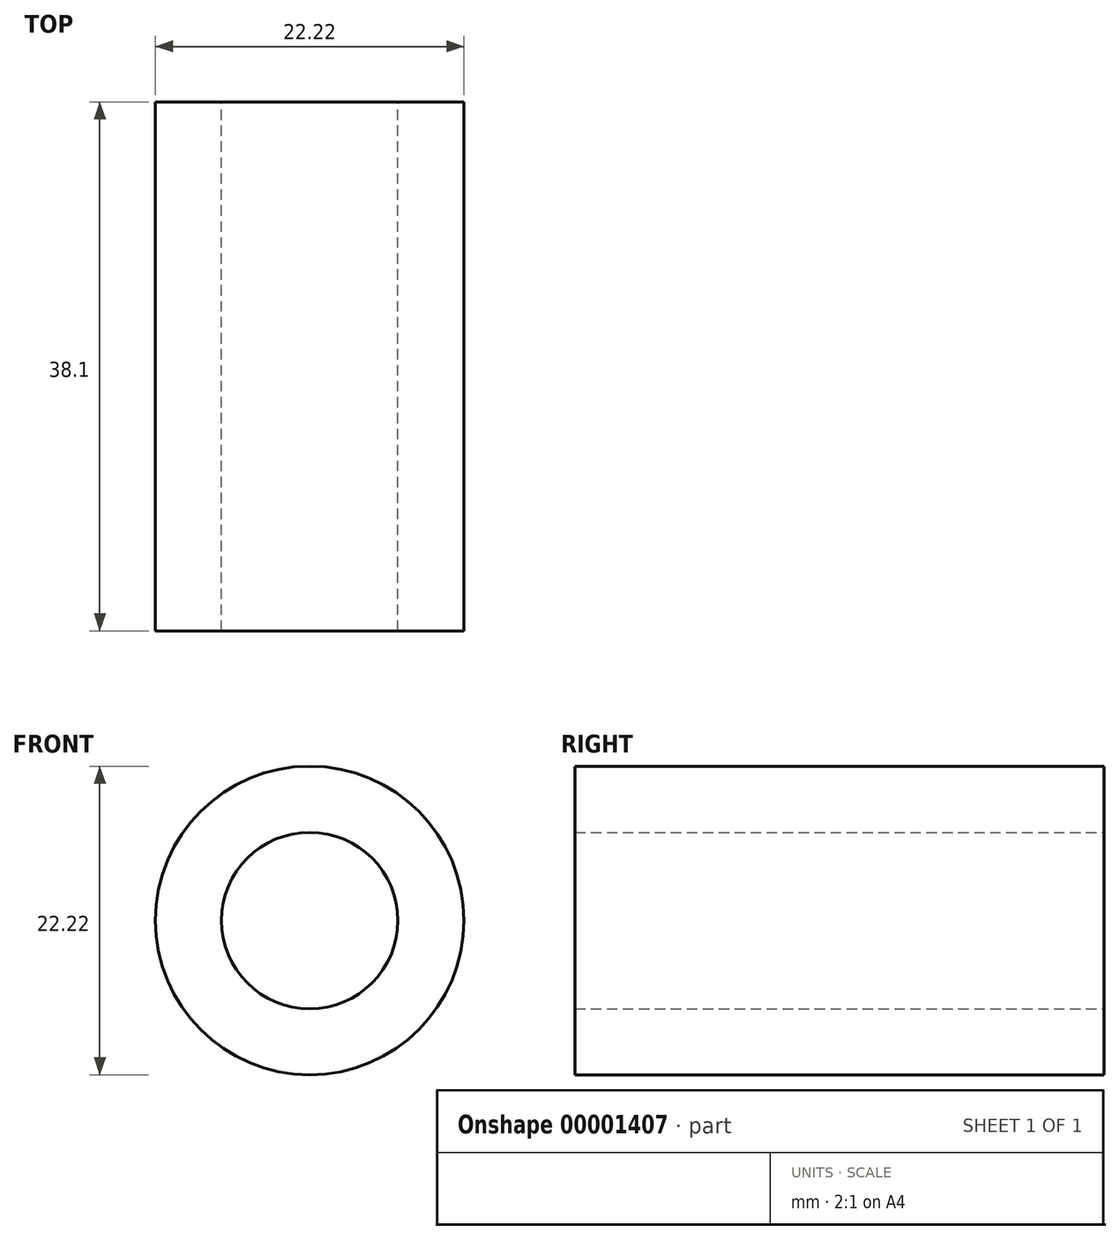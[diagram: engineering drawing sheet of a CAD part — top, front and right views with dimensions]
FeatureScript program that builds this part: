
annotation { "Feature Type Name" : "Feature", "Feature Type Description" : "" }
export const myFeature = defineFeature(function(context is Context, id is Id, definition is map)
    precondition{}
    {
        {
            var Q0;
            Q0=qCreatedBy(makeId("Front.planeOp"),FACE);
            var sketch = newSketch(context, id + "F0", { "sketchPlane" : qUnion([Q0])});
            skCircle(sketch, "E0", {"center": v(0, 0) * mm, "radius": 11.11 * mm});
            skCircle(sketch, "E1", {"center": v(0, 0) * mm, "radius": 6.35 * mm});
            skSolve(sketch);
        }
        {
            var Q0;
            Q0 = qSketchRegion(id + "F0", true);
            extrude(context, id + "F1", {"entities" : qUnion([Q0]), "endBound" : BoundingType.SYMMETRIC, "depth" : 38.1 * mm});
        }
    });
